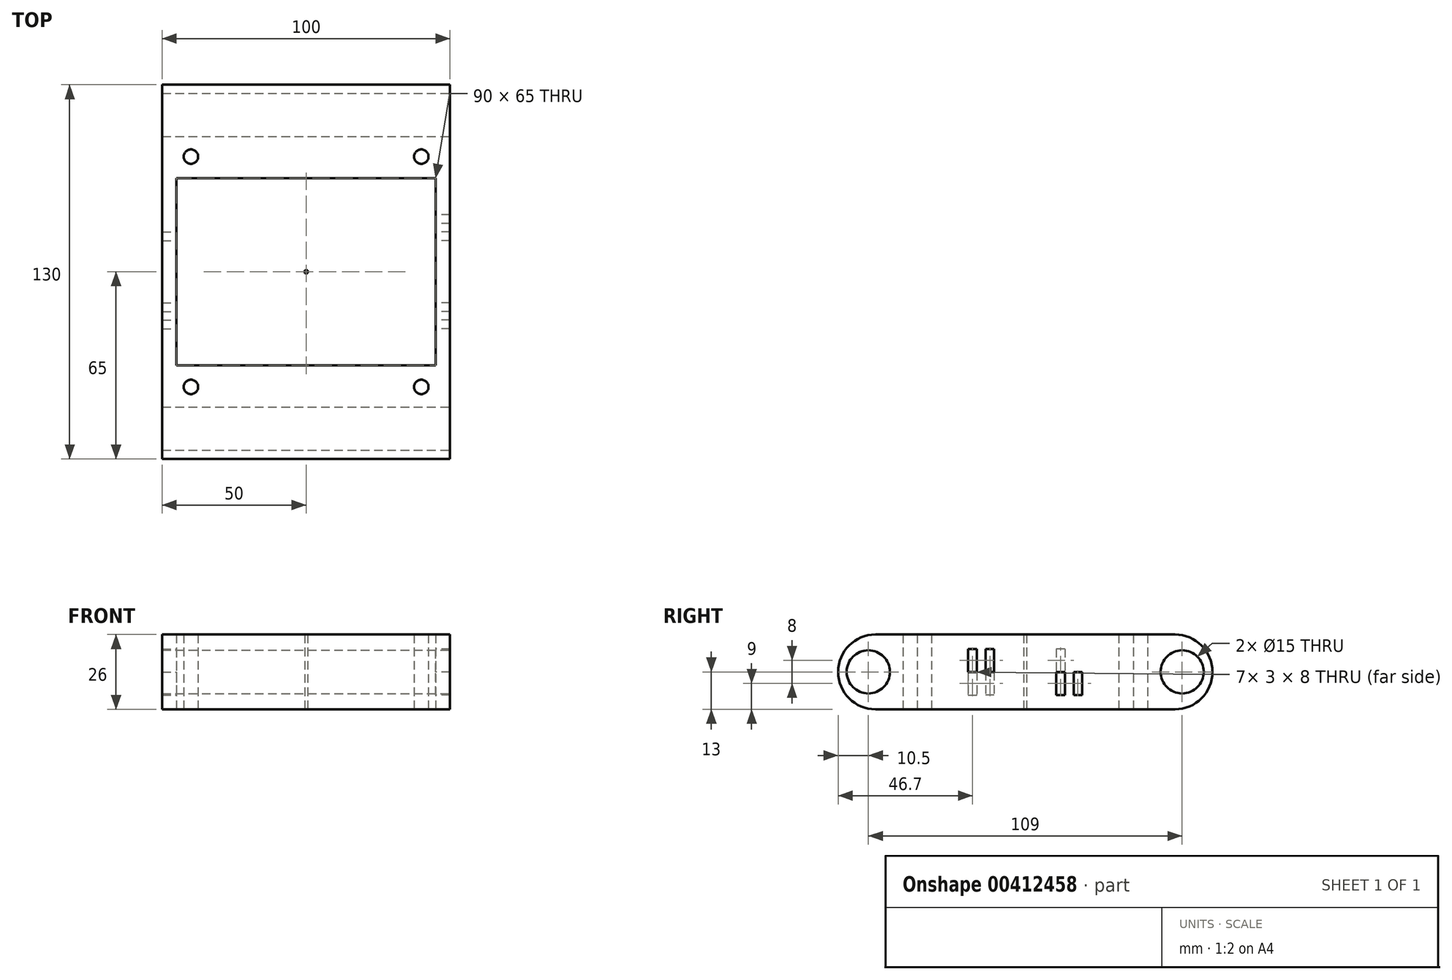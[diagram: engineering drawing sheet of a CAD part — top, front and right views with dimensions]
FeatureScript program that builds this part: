
annotation { "Feature Type Name" : "Feature", "Feature Type Description" : "" }
export const myFeature = defineFeature(function(context is Context, id is Id, definition is map)
    precondition{}
    {
        {
            var Q0;
            Q0=qCreatedBy(makeId("Top.planeOp"),FACE);
            var sketch = newSketch(context, id + "F0", { "sketchPlane" : qUnion([Q0])});
            skLineSegment(sketch, "E0.bottom", {"start": v(50, 65) * mm, "end": v(-50, 65) * mm});
            skLineSegment(sketch, "E0.top", {"start": v(50, -65) * mm, "end": v(-50, -65) * mm});
            skLineSegment(sketch, "E0.left", {"start": v(50, 65) * mm, "end": v(50, -65) * mm});
            skLineSegment(sketch, "E0.right", {"start": v(-50, 65) * mm, "end": v(-50, -65) * mm});
            skPoint(sketch, "E0.middle", {"position": v(0, 0) * mm});
            skLineSegment(sketch, "E1.top", {"start": v(-40, 45) * mm, "end": v(50, 45) * mm});
            skLineSegment(sketch, "E2.top", {"start": v(-40, -45) * mm, "end": v(50, -45) * mm});
            skLineSegment(sketch, "E3.bottom", {"start": v(45, 32.5) * mm, "end": v(-45, 32.5) * mm});
            skLineSegment(sketch, "E3.top", {"start": v(45, -32.5) * mm, "end": v(-45, -32.5) * mm});
            skLineSegment(sketch, "E3.left", {"start": v(45, 32.5) * mm, "end": v(45, -32.5) * mm});
            skLineSegment(sketch, "E3.right", {"start": v(-45, 32.5) * mm, "end": v(-45, -32.5) * mm});
            skCircle(sketch, "E4", {"center": v(-40, 40) * mm, "radius": 2.5 * mm});
            skCircle(sketch, "E5", {"center": v(40, 40) * mm, "radius": 2.5 * mm});
            skCircle(sketch, "E6", {"center": v(40, -40) * mm, "radius": 2.5 * mm});
            skCircle(sketch, "E7", {"center": v(-40, -40) * mm, "radius": 2.5 * mm});
            skLineSegment(sketch, "E8.left", {"start": v(50, 45) * mm, "end": v(50, -34.7) * mm});
            skLineSegment(sketch, "E9.bottom", {"start": v(50, 65) * mm, "end": v(-40, 65) * mm});
            skLineSegment(sketch, "E9.left", {"start": v(50, 65) * mm, "end": v(50, 40) * mm});
            skLineSegment(sketch, "E10.bottom", {"start": v(50, -45) * mm, "end": v(-50, -45) * mm});
            skLineSegment(sketch, "E10.left", {"start": v(50, -45) * mm, "end": v(50, -65) * mm});
            skLineSegment(sketch, "E10.right", {"start": v(-50, -45) * mm, "end": v(-50, -65) * mm});
            skLineSegment(sketch, "E11.bottom", {"start": v(45, 0.5) * mm, "end": v(-45, 0.5) * mm});
            skLineSegment(sketch, "E11.top", {"start": v(45, -0.5) * mm, "end": v(-45, -0.5) * mm});
            skLineSegment(sketch, "E11.left", {"start": v(45, 0.5) * mm, "end": v(45, -0.5) * mm});
            skLineSegment(sketch, "E11.right", {"start": v(-45, 0.5) * mm, "end": v(-45, -0.5) * mm});
            skLineSegment(sketch, "E12.bottom", {"start": v(-0.5, -32.5) * mm, "end": v(0.5, -32.5) * mm});
            skLineSegment(sketch, "E12.top", {"start": v(-0.5, 32.5) * mm, "end": v(0.5, 32.5) * mm});
            skLineSegment(sketch, "E12.left", {"start": v(-0.5, -32.5) * mm, "end": v(-0.5, 32.5) * mm});
            skLineSegment(sketch, "E12.right", {"start": v(0.5, -32.5) * mm, "end": v(0.5, 32.5) * mm});
            skSolve(sketch);
        }
        {
            var Q0;
            {var subQ0=sQuery(id+"F0.wireOp",EDGE,"E0.bottom");Q0=makeQuery(id+"F0.imprint","IMPRINT",FACE,{"disambiguationData":[TD([[makeQuery(id+"F0.imprint","IMPRINT",EDGE,{"derivedFrom":subQ0}),1.0]])]});}
            var Q1;
            Q1=makeQuery(id+"F0.imprint","IMPRINT",FACE,{"disambiguationData":[TD([[makeQuery(id+"F0.imprint","IMPRINT",EDGE,{"derivedFrom":sQuery(id+"F0.wireOp",EDGE,"E1.bottom")}),-1.0]])]});
            var Q2;
            {var subQ0=sQuery(id+"F0.wireOp",EDGE,"E1.top");Q2=makeQuery(id+"F0.imprint","IMPRINT",FACE,{"disambiguationData":[TD([[makeQuery(id+"F0.imprint","IMPRINT",EDGE,{"derivedFrom":subQ0}),-1.0]])]});}
            var Q3;
            Q3=makeQuery(id+"F0.imprint","IMPRINT",FACE,{"disambiguationData":[TD([[makeQuery(id+"F0.imprint","IMPRINT",EDGE,{"derivedFrom":sQuery(id+"F0.wireOp",EDGE,"E2.bottom")}),1.0]])]});
            var Q4;
            {var subQ0=sQuery(id+"F0.wireOp",EDGE,"E0.top");Q4=makeQuery(id+"F0.imprint","IMPRINT",FACE,{"disambiguationData":[TD([[makeQuery(id+"F0.imprint","IMPRINT",EDGE,{"derivedFrom":subQ0}),-1.0]])]});}
            var Q5;
            Q5=makeQuery(id+"F0.imprint","IMPRINT",FACE,{"disambiguationData":[TD([[makeQuery(id+"F0.imprint","IMPRINT",EDGE,{"derivedFrom":sQuery(id+"F0.wireOp",EDGE,"pRW3rzFR-ZSmG-1n1b-oxFP-y6WoqKAtrsM3.bottom")}),1.0]])]});
            var Q6;
            Q6=makeQuery(id+"F0.imprint","IMPRINT",FACE,{"disambiguationData":[TD([[makeQuery(id+"F0.imprint","IMPRINT",EDGE,{"derivedFrom":sQuery(id+"F0.wireOp",EDGE,"E8.bottom")}),-1.0]])]});
            var Q7;
            Q7=makeQuery(id+"F0.imprint","IMPRINT",FACE,{"disambiguationData":[TD([[makeQuery(id+"F0.imprint","IMPRINT",EDGE,{"derivedFrom":sQuery(id+"F0.wireOp",EDGE,"E9.bottom")}),1.0]])]});
            var Q8;
            Q8=makeQuery(id+"F0.imprint","IMPRINT",FACE,{"disambiguationData":[TD([[makeQuery(id+"F0.imprint","IMPRINT",EDGE,{"derivedFrom":sQuery(id+"F0.wireOp",EDGE,"E3.bottom")}),-1.0]])]});
            var Q9;
            Q9=makeQuery(id+"F0.imprint","IMPRINT",FACE,{"disambiguationData":[TD([[makeQuery(id+"F0.imprint","IMPRINT",EDGE,{"derivedFrom":sQuery(id+"F0.wireOp",EDGE,"E10.bottom")}),1.0]])]});
            var Q10;
            Q10=makeQuery(id+"F0.imprint","IMPRINT",FACE,{"disambiguationData":[TD([[makeQuery(id+"F0.imprint","IMPRINT",EDGE,{"derivedFrom":sQuery(id+"F0.wireOp",EDGE,"WSVMbeOV-blDI-kiO2-zCwI-fGnuCaGE87Cd.bottom")}),1.0]])]});
            var Q11;
            Q11=makeQuery(id+"F0.imprint","IMPRINT",FACE,{"disambiguationData":[TD([[makeQuery(id+"F0.imprint","IMPRINT",EDGE,{"derivedFrom":sQuery(id+"F0.wireOp",EDGE,"hR81bXcu-Sj1Q-S8z1-8V7z-bRS3nzz7rQoS.bottom")}),-1.0]])]});
            var Q12;
            {var subQ0=sQuery(id+"F0.wireOp",EDGE,"E11.left");Q12=makeQuery(id+"F0.imprint","IMPRINT",FACE,{"disambiguationData":[TD([[makeQuery(id+"F0.imprint","IMPRINT",EDGE,{"derivedFrom":subQ0}),-1.0]])]});}
            var Q13;
            {var subQ0=sQuery(id+"F0.wireOp",EDGE,"E11.right");Q13=makeQuery(id+"F0.imprint","IMPRINT",FACE,{"disambiguationData":[TD([[makeQuery(id+"F0.imprint","IMPRINT",EDGE,{"derivedFrom":subQ0}),1.0]])]});}
            var Q14;
            {var subQ0=sQuery(id+"F0.wireOp",EDGE,"E12.right");var subQ1=sQuery(id+"F0.wireOp",EDGE,"E11.bottom");var subQ2=makeQuery(id+"F0.imprint","INTERSECT",VERTEX,{"derivedFrom":[subQ1,subQ0]});Q14=makeQuery(id+"F0.imprint","IMPRINT",FACE,{"disambiguationData":[TD([[makeQuery(id+"F0.imprint","IMPRINT",EDGE,{"disambiguationData":[TD([[subQ2,-1.0]])],"derivedFrom":subQ1}),1.0]])]});}
            var Q15;
            {var subQ5=sQuery(id+"F0.wireOp",EDGE,"E12.bottom");Q15=makeQuery(id+"F0.imprint","IMPRINT",FACE,{"disambiguationData":[TD([[makeQuery(id+"F0.imprint","IMPRINT",EDGE,{"derivedFrom":subQ5}),1.0]])]});}
            var Q16;
            {var subQ5=sQuery(id+"F0.wireOp",EDGE,"E12.top");Q16=makeQuery(id+"F0.imprint","IMPRINT",FACE,{"disambiguationData":[TD([[makeQuery(id+"F0.imprint","IMPRINT",EDGE,{"derivedFrom":subQ5}),-1.0]])]});}
            extrude(context, id + "F1", {"entities" : qUnion([Q0, Q1, Q2, Q3, Q4, Q5, Q6, Q7, Q8, Q9, Q10, Q11, Q12, Q13, Q14, Q15, Q16]), "endBound" : BoundingType.SYMMETRIC, "depth" : 26 * mm});
        }
        {
            var Q0;
            Q0=qCreatedBy(makeId("Right.planeOp"),FACE);
            var sketch = newSketch(context, id + "F2", { "sketchPlane" : qUnion([Q0])});
            skLineSegment(sketch, "E13.bottom", {"start": v(65, 13) * mm, "end": v(-65, 13) * mm});
            skLineSegment(sketch, "E13.top", {"start": v(65, -13) * mm, "end": v(-65, -13) * mm});
            skLineSegment(sketch, "E13.left", {"start": v(65, 13) * mm, "end": v(65, -13) * mm});
            skLineSegment(sketch, "E13.right", {"start": v(-65, 13) * mm, "end": v(-65, -13) * mm});
            skPoint(sketch, "E13.middle", {"position": v(0, 0) * mm});
            skCircle(sketch, "E14", {"center": v(54.5, 0) * mm, "radius": 7.5 * mm});
            skCircle(sketch, "E15", {"center": v(-54.5, 0) * mm, "radius": 7.5 * mm});
            skLineSegment(sketch, "E16.bottom", {"start": v(19.8, 0) * mm, "end": v(16.8, 0) * mm});
            skLineSegment(sketch, "E16.top", {"start": v(19.8, -8) * mm, "end": v(16.8, -8) * mm});
            skLineSegment(sketch, "E16.left", {"start": v(19.8, 0) * mm, "end": v(19.8, -8) * mm});
            skLineSegment(sketch, "E16.right", {"start": v(16.8, 0) * mm, "end": v(16.8, -8) * mm});
            skLineSegment(sketch, "E17.bottom", {"start": v(-16.8, 8) * mm, "end": v(-19.8, 8) * mm});
            skLineSegment(sketch, "E17.top", {"start": v(-16.8, 0) * mm, "end": v(-19.8, 0) * mm});
            skLineSegment(sketch, "E17.left", {"start": v(-16.8, 8) * mm, "end": v(-16.8, 0) * mm});
            skLineSegment(sketch, "E17.right", {"start": v(-19.8, 8) * mm, "end": v(-19.8, 0) * mm});
            skLineSegment(sketch, "E18.MirrorCS", {"start": v(-16.8, 0) * mm, "end": v(-16.8, -8) * mm});
            skLineSegment(sketch, "E19.MirrorCS", {"start": v(-19.8, 0) * mm, "end": v(-16.8, 0) * mm});
            skLineSegment(sketch, "E20.MirrorCS", {"start": v(-19.8, -8) * mm, "end": v(-16.8, -8) * mm});
            skLineSegment(sketch, "E21.MirrorCS", {"start": v(-19.8, 0) * mm, "end": v(-19.8, -8) * mm});
            skLineSegment(sketch, "E22.MirrorCS", {"start": v(16.8, 0) * mm, "end": v(19.8, 0) * mm});
            skLineSegment(sketch, "E23.MirrorCS", {"start": v(16.8, 8) * mm, "end": v(19.8, 8) * mm});
            skLineSegment(sketch, "E24.MirrorCS", {"start": v(19.8, 8) * mm, "end": v(19.8, 0) * mm});
            skLineSegment(sketch, "E25.MirrorCS", {"start": v(16.8, 8) * mm, "end": v(16.8, 0) * mm});
            skLineSegment(sketch, "E26.bottom", {"start": v(13.8, 0) * mm, "end": v(10.8, 0) * mm});
            skLineSegment(sketch, "E26.top", {"start": v(13.8, -8) * mm, "end": v(10.8, -8) * mm});
            skLineSegment(sketch, "E26.left", {"start": v(13.8, 0) * mm, "end": v(13.8, -8) * mm});
            skLineSegment(sketch, "E26.right", {"start": v(10.8, 0) * mm, "end": v(10.8, -8) * mm});
            skLineSegment(sketch, "E27.bottom", {"start": v(13.8, 8) * mm, "end": v(10.8, 8) * mm});
            skLineSegment(sketch, "E27.left", {"start": v(13.8, 8) * mm, "end": v(13.8, 0) * mm});
            skLineSegment(sketch, "E27.right", {"start": v(10.8, 8) * mm, "end": v(10.8, 0) * mm});
            skLineSegment(sketch, "E28.bottom", {"start": v(-10.8, 8) * mm, "end": v(-13.8, 8) * mm});
            skLineSegment(sketch, "E28.top", {"start": v(-10.8, 0) * mm, "end": v(-13.8, 0) * mm});
            skLineSegment(sketch, "E28.left", {"start": v(-10.8, 8) * mm, "end": v(-10.8, 0) * mm});
            skLineSegment(sketch, "E28.right", {"start": v(-13.8, 8) * mm, "end": v(-13.8, 0) * mm});
            skLineSegment(sketch, "E29.top", {"start": v(-10.8, -8) * mm, "end": v(-13.8, -8) * mm});
            skLineSegment(sketch, "E29.left", {"start": v(-10.8, 0) * mm, "end": v(-10.8, -8) * mm});
            skLineSegment(sketch, "E29.right", {"start": v(-13.8, 0) * mm, "end": v(-13.8, -8) * mm});
            skSolve(sketch);
        }
        {
            var Q0;
            Q0=makeQuery(id+"F2.imprint","IMPRINT",FACE,{"disambiguationData":[TD([[makeQuery(id+"F2.imprint","IMPRINT",EDGE,{"derivedFrom":sQuery(id+"F2.wireOp",EDGE,"E14")}),1.0]])]});
            var Q1;
            Q1=makeQuery(id+"F2.imprint","IMPRINT",FACE,{"disambiguationData":[TD([[makeQuery(id+"F2.imprint","IMPRINT",EDGE,{"derivedFrom":sQuery(id+"F2.wireOp",EDGE,"E15")}),1.0]])]});
            extrude(context, id + "F3", {"entities" : qUnion([Q0, Q1]), "operationType" : NewBodyOperationType.REMOVE, "endBound" : BoundingType.SYMMETRIC, "oppositeDirection" : true, "depth" : 100 * mm});
        }
        {
            var Q0;
            Q0=makeQuery(id+"F1.opExtrude","CAP_EDGE",EDGE,{"disambiguationData":[OSD([sQuery(id+"F0.wireOp",EDGE,"E0.bottom"),sQuery(id+"F0.wireOp",EDGE,"E9.bottom")])],"isStart":false});
            var Q1;
            Q1=makeQuery(id+"F1.opExtrude","CAP_EDGE",EDGE,{"disambiguationData":[OSD([sQuery(id+"F0.wireOp",EDGE,"E0.bottom"),sQuery(id+"F0.wireOp",EDGE,"E9.bottom")])],"isStart":true});
            var Q2;
            Q2=makeQuery(id+"F1.opExtrude","CAP_EDGE",EDGE,{"disambiguationData":[OSD([sQuery(id+"F0.wireOp",EDGE,"E0.top")])],"isStart":false});
            var Q3;
            Q3=makeQuery(id+"F1.opExtrude","CAP_EDGE",EDGE,{"disambiguationData":[OSD([sQuery(id+"F0.wireOp",EDGE,"E0.top")])],"isStart":true});
            fillet(context, id + "F4", {"entities" : qUnion([Q0, Q1, Q2, Q3]), "radius" : 13 * mm, "tangentPropagation" : true, "allowEdgeOverflow" : false});
        }
        {
            var Q0;
            Q0=makeQuery(id+"F2.imprint","IMPRINT",FACE,{"disambiguationData":[TD([[makeQuery(id+"F2.imprint","IMPRINT",EDGE,{"derivedFrom":sQuery(id+"F2.wireOp",EDGE,"E18.MirrorCS")}),-1.0]])]});
            var Q1;
            Q1=makeQuery(id+"F2.imprint","IMPRINT",FACE,{"disambiguationData":[TD([[makeQuery(id+"F2.imprint","IMPRINT",EDGE,{"derivedFrom":sQuery(id+"F2.wireOp",EDGE,"E28.top")}),1.0]])]});
            var Q2;
            Q2=makeQuery(id+"F2.imprint","IMPRINT",FACE,{"disambiguationData":[TD([[makeQuery(id+"F2.imprint","IMPRINT",EDGE,{"derivedFrom":sQuery(id+"F2.wireOp",EDGE,"E27.bottom")}),1.0]])]});
            var Q3;
            Q3=makeQuery(id+"F2.imprint","IMPRINT",FACE,{"disambiguationData":[TD([[makeQuery(id+"F2.imprint","IMPRINT",EDGE,{"derivedFrom":sQuery(id+"F2.wireOp",EDGE,"E22.MirrorCS")}),1.0]])]});
            extrude(context, id + "F5", {"entities" : qUnion([Q0, Q1, Q2, Q3]), "operationType" : NewBodyOperationType.REMOVE, "oppositeDirection" : true, "depth" : 50 * mm});
        }
        {
            var Q0;
            Q0=makeQuery(id+"F2.imprint","IMPRINT",FACE,{"disambiguationData":[TD([[makeQuery(id+"F2.imprint","IMPRINT",EDGE,{"derivedFrom":sQuery(id+"F2.wireOp",EDGE,"E26.bottom")}),1.0]])]});
            var Q1;
            Q1=makeQuery(id+"F2.imprint","IMPRINT",FACE,{"disambiguationData":[TD([[makeQuery(id+"F2.imprint","IMPRINT",EDGE,{"derivedFrom":sQuery(id+"F2.wireOp",EDGE,"E16.bottom")}),1.0]])]});
            var Q2;
            Q2=makeQuery(id+"F2.imprint","IMPRINT",FACE,{"disambiguationData":[TD([[makeQuery(id+"F2.imprint","IMPRINT",EDGE,{"derivedFrom":sQuery(id+"F2.wireOp",EDGE,"E28.bottom")}),1.0]])]});
            var Q3;
            Q3=makeQuery(id+"F2.imprint","IMPRINT",FACE,{"disambiguationData":[TD([[makeQuery(id+"F2.imprint","IMPRINT",EDGE,{"derivedFrom":sQuery(id+"F2.wireOp",EDGE,"E17.bottom")}),1.0]])]});
            var Q4;
            Q4=makeQuery(id+"F2.imprint","IMPRINT",FACE,{"disambiguationData":[TD([[makeQuery(id+"F2.imprint","IMPRINT",EDGE,{"derivedFrom":sQuery(id+"F2.wireOp",EDGE,"E26.top")}),-1.0]])]});
            var Q5;
            Q5=makeQuery(id+"F2.imprint","IMPRINT",FACE,{"disambiguationData":[TD([[makeQuery(id+"F2.imprint","IMPRINT",EDGE,{"derivedFrom":sQuery(id+"F2.wireOp",EDGE,"E16.top")}),-1.0]])]});
            extrude(context, id + "F6", {"entities" : qUnion([Q0, Q1, Q2, Q3, Q4, Q5]), "operationType" : NewBodyOperationType.REMOVE, "depth" : 50 * mm, "hasSecondDirection" : true, "secondDirectionOppositeDirection" : true, "secondDirectionDepth" : 25 * mm});
        }
    });
